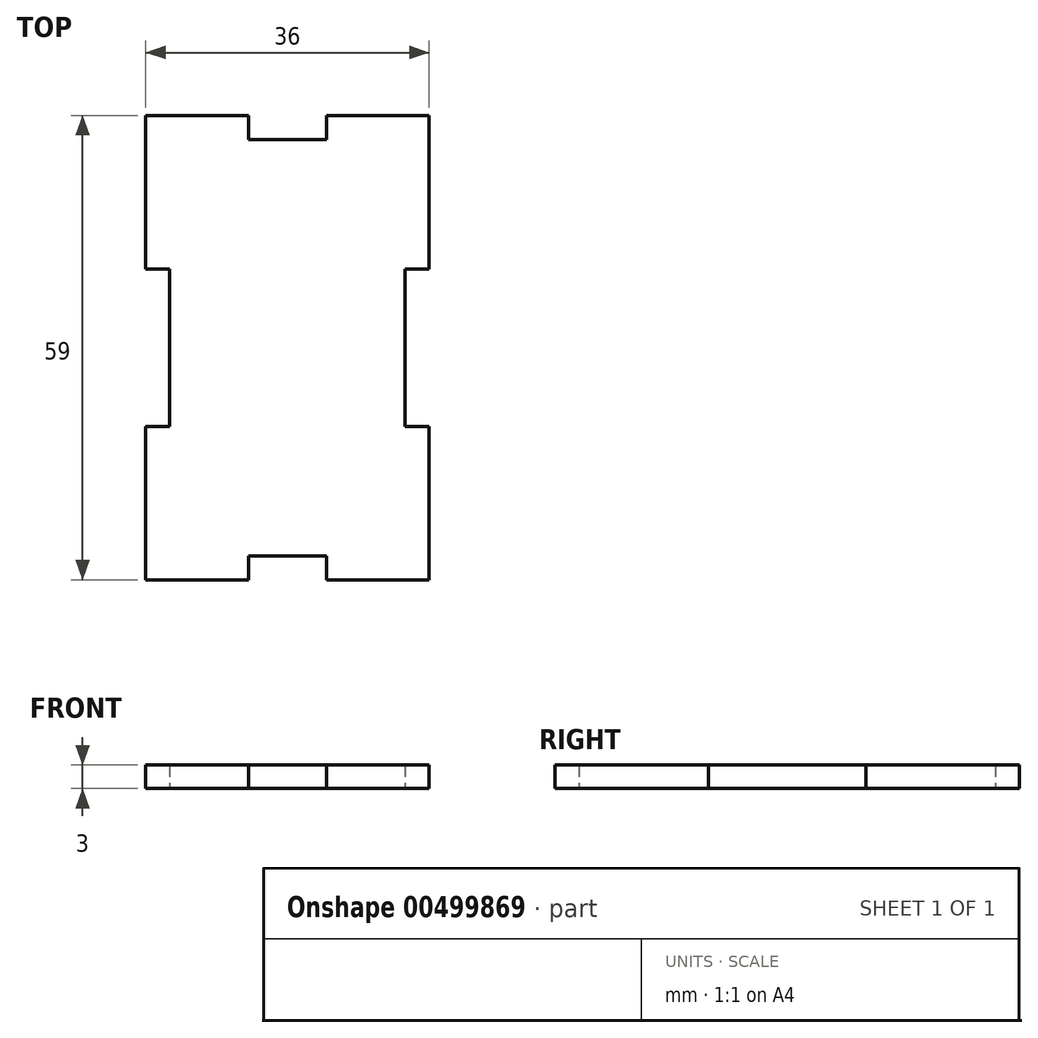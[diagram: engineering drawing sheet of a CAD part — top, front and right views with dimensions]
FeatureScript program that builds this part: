
annotation { "Feature Type Name" : "Feature", "Feature Type Description" : "" }
export const myFeature = defineFeature(function(context is Context, id is Id, definition is map)
    precondition{}
    {
        {
            var Q0;
            Q0=qCreatedBy(makeId("Top.planeOp"),FACE);
            var sketch = newSketch(context, id + "F0", { "sketchPlane" : qUnion([Q0])});
            skLineSegment(sketch, "E0.bottom", {"start": v(18, -29.5) * mm, "end": v(-18, -29.5) * mm});
            skLineSegment(sketch, "E0.top", {"start": v(18, 29.5) * mm, "end": v(-18, 29.5) * mm});
            skLineSegment(sketch, "E0.left", {"start": v(18, -29.5) * mm, "end": v(18, 29.5) * mm});
            skLineSegment(sketch, "E0.right", {"start": v(-18, -29.5) * mm, "end": v(-18, 29.5) * mm});
            skPoint(sketch, "E0.middle", {"position": v(0, 0) * mm});
            skLineSegment(sketch, "E1.bottom", {"start": v(-14.95, 10) * mm, "end": v(-18, 10) * mm});
            skLineSegment(sketch, "E1.top", {"start": v(-14.95, -10) * mm, "end": v(-18, -10) * mm});
            skLineSegment(sketch, "E1.left", {"start": v(-14.95, 10) * mm, "end": v(-14.95, -10) * mm});
            skLineSegment(sketch, "E1.right", {"start": v(-18, 10) * mm, "end": v(-18, -10) * mm});
            skPoint(sketch, "E1.middle", {"position": v(-16.48, 0) * mm});
            skLineSegment(sketch, "E2.bottom", {"start": v(18, -10) * mm, "end": v(14.95, -10) * mm});
            skLineSegment(sketch, "E2.top", {"start": v(18, 10) * mm, "end": v(14.95, 10) * mm});
            skLineSegment(sketch, "E2.left", {"start": v(18, -10) * mm, "end": v(18, 10) * mm});
            skLineSegment(sketch, "E2.right", {"start": v(14.95, -10) * mm, "end": v(14.95, 10) * mm});
            skPoint(sketch, "E2.middle", {"position": v(16.47, 0) * mm});
            skLineSegment(sketch, "E3.bottom", {"start": v(4.95, 26.45) * mm, "end": v(-4.95, 26.45) * mm});
            skLineSegment(sketch, "E3.top", {"start": v(4.95, 29.5) * mm, "end": v(-4.95, 29.5) * mm});
            skLineSegment(sketch, "E3.left", {"start": v(4.95, 26.45) * mm, "end": v(4.95, 29.5) * mm});
            skLineSegment(sketch, "E3.right", {"start": v(-4.95, 26.45) * mm, "end": v(-4.95, 29.5) * mm});
            skPoint(sketch, "E3.middle", {"position": v(0, 27.97) * mm});
            skLineSegment(sketch, "E4.bottom", {"start": v(4.95, -29.5) * mm, "end": v(-4.95, -29.5) * mm});
            skLineSegment(sketch, "E4.top", {"start": v(4.95, -26.45) * mm, "end": v(-4.95, -26.45) * mm});
            skLineSegment(sketch, "E4.left", {"start": v(4.95, -29.5) * mm, "end": v(4.95, -26.45) * mm});
            skLineSegment(sketch, "E4.right", {"start": v(-4.95, -29.5) * mm, "end": v(-4.95, -26.45) * mm});
            skPoint(sketch, "E4.middle", {"position": v(0, -27.97) * mm});
            skSolve(sketch);
        }
        {
            var Q0;
            {var subQ6=sQuery(id+"F0.wireOp",EDGE,"E0.bottom");Q0=makeQuery(id+"F0.imprint","IMPRINT",FACE,{"disambiguationData":[TD([[makeQuery(id+"F0.imprint","IMPRINT",EDGE,{"derivedFrom":subQ6}),-1.0]])]});}
            extrude(context, id + "F1", {"entities" : qUnion([Q0]), "depth" : 3 * mm, "offsetDistance" : 25 * mm});
        }
    });
